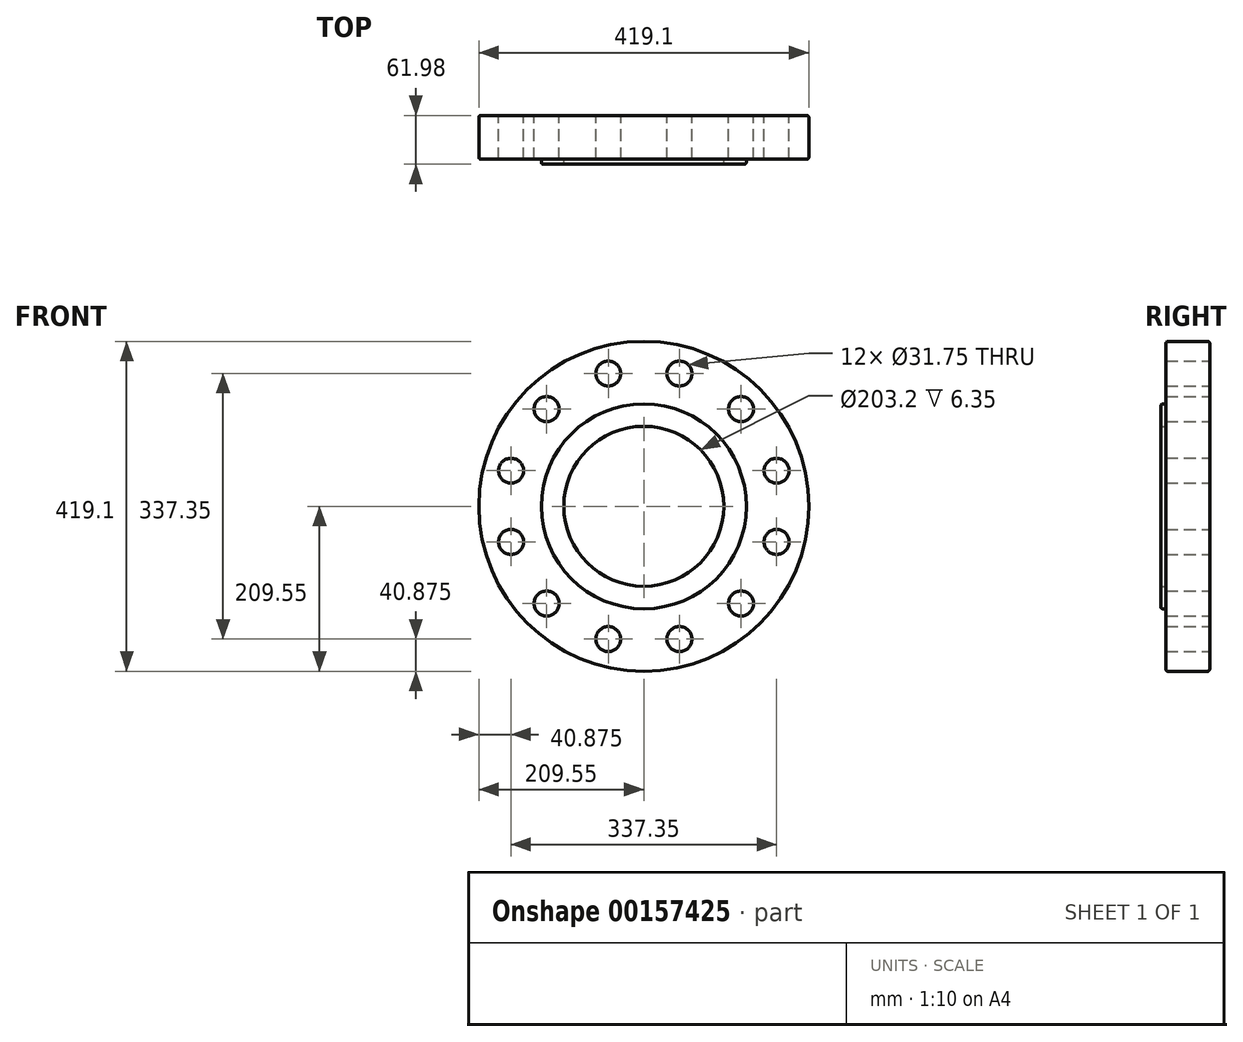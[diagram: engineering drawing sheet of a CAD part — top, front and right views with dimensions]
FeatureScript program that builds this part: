
annotation { "Feature Type Name" : "Feature", "Feature Type Description" : "" }
export const myFeature = defineFeature(function(context is Context, id is Id, definition is map)
    precondition{}
    {
        {
            var Q0;
            Q0=qCreatedBy(makeId("Front.planeOp"),FACE);
            var sketch = newSketch(context, id + "F0", { "sketchPlane" : qUnion([Q0])});
            skCircle(sketch, "E0", {"center": v(0, 0) * mm, "radius": 209.55 * mm});
            skCircle(sketch, "E1", {"center": v(45.2, 168.67) * mm, "radius": 15.88 * mm});
            skCircle(sketch, "E2.1.0", {"center": v(-45.2, 168.67) * mm, "radius": 15.88 * mm});
            skCircle(sketch, "E2.2.0", {"center": v(-123.48, 123.48) * mm, "radius": 15.88 * mm});
            skCircle(sketch, "E2.3.0", {"center": v(-168.67, 45.2) * mm, "radius": 15.88 * mm});
            skCircle(sketch, "E2.4.0", {"center": v(-168.67, -45.2) * mm, "radius": 15.88 * mm});
            skCircle(sketch, "E2.5.0", {"center": v(-123.48, -123.48) * mm, "radius": 15.88 * mm});
            skCircle(sketch, "E2.6.0", {"center": v(-45.2, -168.67) * mm, "radius": 15.88 * mm});
            skCircle(sketch, "E2.7.0", {"center": v(45.2, -168.67) * mm, "radius": 15.88 * mm});
            skCircle(sketch, "E2.8.0", {"center": v(123.48, -123.48) * mm, "radius": 15.88 * mm});
            skCircle(sketch, "E2.9.0", {"center": v(168.67, -45.2) * mm, "radius": 15.88 * mm});
            skCircle(sketch, "E2.10.0", {"center": v(168.67, 45.2) * mm, "radius": 15.88 * mm});
            skCircle(sketch, "E2.11.0", {"center": v(123.48, 123.48) * mm, "radius": 15.88 * mm});
            skSolve(sketch);
        }
        {
            var Q0;
            Q0=qSketchRegion(id+"F0",true);
            extrude(context, id + "F1", {"entities" : qUnion([Q0]), "depth" : 55.63 * mm});
        }
        {
            var Q0;
            Q0=makeQuery(id+"F1.opExtrude","CAP_FACE",FACE,{"disambiguationData":[OSD([sQuery(id+"F0.wireOp",EDGE,"E0"),sQuery(id+"F0.wireOp",EDGE,"N24dluJ5-ltBv-c6OA-tLs4-8FkM38SAwfNM"),sQuery(id+"F0.wireOp",EDGE,"E1"),sQuery(id+"F0.wireOp",EDGE,"E2.1.0"),sQuery(id+"F0.wireOp",EDGE,"E2.2.0"),sQuery(id+"F0.wireOp",EDGE,"E2.3.0"),sQuery(id+"F0.wireOp",EDGE,"E2.4.0"),sQuery(id+"F0.wireOp",EDGE,"E2.5.0"),sQuery(id+"F0.wireOp",EDGE,"E2.6.0"),sQuery(id+"F0.wireOp",EDGE,"E2.7.0"),sQuery(id+"F0.wireOp",EDGE,"E2.8.0"),sQuery(id+"F0.wireOp",EDGE,"E2.9.0"),sQuery(id+"F0.wireOp",EDGE,"E2.10.0"),sQuery(id+"F0.wireOp",EDGE,"E2.11.0")])],"isStart":false});
            var sketch = newSketch(context, id + "F2", { "sketchPlane" : qUnion([Q0])});
            skCircle(sketch, "E3", {"center": v(0, 0) * mm, "radius": 130.18 * mm});
            skCircle(sketch, "E4", {"center": v(0, 0) * mm, "radius": 101.6 * mm});
            skSolve(sketch);
        }
        {
            var Q0;
            Q0=qSketchRegion(id+"F2",true);
            extrude(context, id + "F3", {"entities" : qUnion([Q0]), "operationType" : NewBodyOperationType.ADD, "depth" : 6.35 * mm});
        }
        {
            var Q0;
            Q0=makeQuery(id+"F1.opExtrude","CAP_EDGE",EDGE,{"disambiguationData":[OSD([sQuery(id+"F0.wireOp",EDGE,"E0")])],"isStart":false});
            var Q1;
            Q1=makeQuery(id+"F1.opExtrude","CAP_EDGE",EDGE,{"disambiguationData":[OSD([sQuery(id+"F0.wireOp",EDGE,"E0")])],"isStart":true});
            var Q2;
            Q2=makeQuery(id+"F3.opExtrude","CAP_EDGE",EDGE,{"disambiguationData":[OSD([sQuery(id+"F2.wireOp",EDGE,"E3")])],"isStart":false});
            var Q3;
            Q3=makeQuery(id+"F3.opExtrude","CAP_EDGE",EDGE,{"disambiguationData":[OSD([sQuery(id+"F2.wireOp",EDGE,"E3")])],"isStart":true});
            fillet(context, id + "F4", {"entities" : qUnion([Q0, Q1, Q2, Q3]), "radius" : 2.54 * mm, "tangentPropagation" : true, "allowEdgeOverflow" : false});
        }
    });
